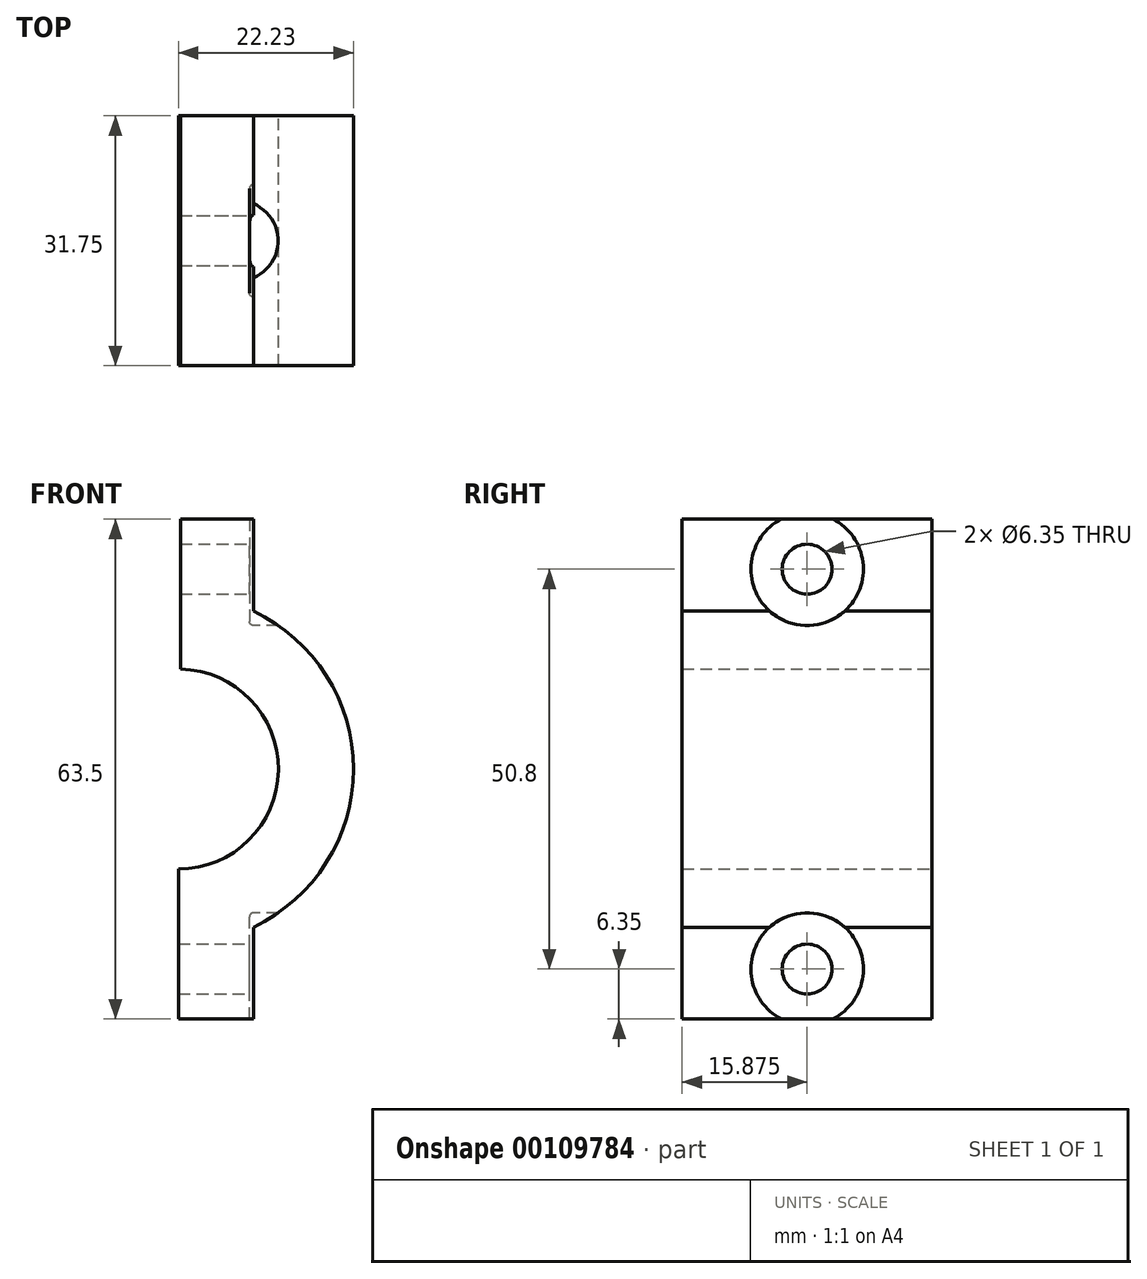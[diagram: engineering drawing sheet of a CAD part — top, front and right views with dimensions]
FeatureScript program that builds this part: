
annotation { "Feature Type Name" : "Feature", "Feature Type Description" : "" }
export const myFeature = defineFeature(function(context is Context, id is Id, definition is map)
    precondition{}
    {
        {
            var Q0;
            Q0=qCreatedBy(makeId("Front.planeOp"),FACE);
            var sketch = newSketch(context, id + "F0", { "sketchPlane" : qUnion([Q0])});
            skArc(sketch, "E0", {"start": v(0, -12.7) * mm, "mid": v(12.7, 0) * mm, "end": v(0, 12.7) * mm});
            skArc(sketch, "E1", {"start": v(9.52, -20.08) * mm, "mid": v(22.23, 0) * mm, "end": v(9.53, 20.08) * mm});
            skLineSegment(sketch, "E2.bottom", {"start": v(0, 31.75) * mm, "end": v(9.52, 31.75) * mm});
            skLineSegment(sketch, "E2.top", {"start": v(0, -31.75) * mm, "end": v(9.53, -31.75) * mm});
            skLineSegment(sketch, "E2.left", {"start": v(0, 31.75) * mm, "end": v(0, 12.7) * mm});
            skLineSegment(sketch, "E2.right", {"start": v(9.53, 31.75) * mm, "end": v(9.53, 20.08) * mm});
            skLineSegment(sketch, "E3.trimOffspring", {"start": v(0, -12.7) * mm, "end": v(0, -31.75) * mm});
            skLineSegment(sketch, "E4.trimOffspring", {"start": v(9.53, -20.08) * mm, "end": v(9.53, -31.75) * mm});
            skSolve(sketch);
        }
        {
            var Q0;
            Q0 = qSketchRegion(id + "F0", true);
            extrude(context, id + "F1", {"entities" : qUnion([Q0]), "depth" : 31.75 * mm});
        }
        {
            var Q0;
            Q0=makeQuery(id+"F1.opExtrude","SWEPT_FACE",FACE,{"disambiguationData":[OSD([sQuery(id+"F0.wireOp",EDGE,"E2.right")])]});
            var sketch = newSketch(context, id + "F2", { "sketchPlane" : qUnion([Q0])});
            skCircle(sketch, "E5", {"center": v(-15.88, -25.4) * mm, "radius": 3.18 * mm});
            skCircle(sketch, "E6", {"center": v(-15.88, 25.4) * mm, "radius": 3.18 * mm});
            skSolve(sketch);
        }
        {
            var Q0;
            Q0 = qSketchRegion(id + "F2", true);
            extrude(context, id + "F3", {"entities" : qUnion([Q0]), "operationType" : NewBodyOperationType.REMOVE, "oppositeDirection" : true, "depth" : 25.4 * mm});
        }
        {
            var Q0;
            Q0=makeQuery(id+"F1.opExtrude","SWEPT_FACE",FACE,{"disambiguationData":[OSD([sQuery(id+"F0.wireOp",EDGE,"E2.right")])]});
            var sketch = newSketch(context, id + "F4", { "sketchPlane" : qUnion([Q0])});
            skCircle(sketch, "E7", {"center": v(-15.88, 25.4) * mm, "radius": 7.14 * mm});
            skCircle(sketch, "E8", {"center": v(-15.88, -25.4) * mm, "radius": 7.14 * mm});
            skSolve(sketch);
        }
        {
            var Q0;
            Q0 = qSketchRegion(id + "F4", true);
            extrude(context, id + "F5", {"entities" : qUnion([Q0]), "operationType" : NewBodyOperationType.REMOVE, "depth" : 25.4 * mm, "hasSecondDirection" : true, "secondDirectionOppositeDirection" : true, "secondDirectionDepth" : 0.5 * mm});
        }
        {
            var Q0;
            Q0=makeQuery(id+"F5.boolean.opBoolean","COPY",EDGE,{"derivedFrom":makeQuery(id+"F5.opExtrude","CAP_EDGE",EDGE,{"disambiguationData":[OSD([sQuery(id+"F4.wireOp",EDGE,"E7")])],"isStart":true})});
            var Q1;
            Q1=makeQuery(id+"F5.boolean.opBoolean","COPY",EDGE,{"derivedFrom":makeQuery(id+"F5.opExtrude","CAP_EDGE",EDGE,{"disambiguationData":[OSD([sQuery(id+"F4.wireOp",EDGE,"E8")])],"isStart":true})});
            fillet(context, id + "F6", {"entities" : qUnion([Q0, Q1]), "radius" : 0.5 * mm, "tangentPropagation" : true, "allowEdgeOverflow" : false});
        }
        {
            var Q0;
            Q0=qCreatedBy(makeId("Front.planeOp"),FACE);
            var sketch = newSketch(context, id + "F7", { "sketchPlane" : qUnion([Q0])});
            skLineSegment(sketch, "E9.bottom", {"start": v(-0.94, 32.46) * mm, "end": v(0.25, 32.46) * mm});
            skLineSegment(sketch, "E9.top", {"start": v(-0.94, 11.94) * mm, "end": v(0.25, 11.94) * mm});
            skLineSegment(sketch, "E9.left", {"start": v(-0.94, 32.46) * mm, "end": v(-0.94, 11.94) * mm});
            skLineSegment(sketch, "E9.right", {"start": v(0.25, 32.46) * mm, "end": v(0.25, 11.94) * mm});
            skSolve(sketch);
        }
        {
            var Q0;
            Q0=makeQuery(id+"F7.imprint","IMPRINT",FACE,{"disambiguationData":[TD([[makeQuery(id+"F7.imprint","IMPRINT",EDGE,{"derivedFrom":sQuery(id+"F7.wireOp",EDGE,"E9.bottom")}),-1.0]])]});
            extrude(context, id + "F8", {"entities" : qUnion([Q0]), "operationType" : NewBodyOperationType.REMOVE, "depth" : 38.1 * mm});
        }
    });
